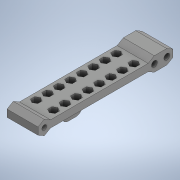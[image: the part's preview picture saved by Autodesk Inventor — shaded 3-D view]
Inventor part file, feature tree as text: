
AUTODESK INVENTOR PART (.ipt)
format: ipt  version: 2020 (Build 240168000, 168)  size: 555,008 bytes
history: native  units: in
note: dims shown in document units (in); Inventor stores cm internally (conversion verified against a paired STEP export)
features: sketch x7, extrude x6, projected_geometry x4, plane x2, mirror x1, fillet x1
ambient origin geometry x8: Origin, YZ Plane, XZ Plane, XY Plane, X Axis, Y Axis, Z Axis, Center Point
bodies: Solid1 (feature_tree)
feature tree (21):
  extrude  "Extrusion1"  Depth=3.4256in
  plane  "Work Plane1"
  extrude  "Extrusion2"  Depth=0.7874in
  sketch  "Sketch4"  dims[d4=0.0in d5=0.0906in]
  extrude  "Extrusion4"  Depth=0.0906in
  plane  "Work Plane2"
  extrude  "Extrusion6"  Depth=3.1106in
  mirror  "Mirror2"
  extrude  "Extrusion7"  Depth=0.315in
  extrude  "Extrusion8"  Depth=0.2362in
  fillet  "Fillet1"  [1 undecoded]
  sketch  "Sketch1"  dims[d0=0.1818in d1=3.4256in]
  sketch  "Sketch2"  dims[d2=0.122in d3=0.7874in]
  sketch  "Sketch5"  dims[d6=0.7874in d7=0.0in d28=3.1106in]
  sketch  "Sketch7"  dims[d29=0.315in d31=0.315in]
  projected_geometry  "Projected Loop7"
  projected_geometry  "Projected Loop8"
  sketch  "Sketch8"  dims[d33=0.1476in d34=0.2362in d35=0.0in]
  projected_geometry  "Projected Loop9"
  sketch  "Sketch10"  dims[d38=0.315in d39=0.2756in d40=-0.3092in d41=0.0787in d42=0.0787in d43=0.0787in d44=3.1496in d46=0.2913in d47=0.3937in d49=0.3937in d51=3.1496in d53=0.2913in d54=0.3937in d56=0.3937in d58=0.0in d59=0.0in d60=1.0994in d61=0.1378in d63=1.1811in d64=0.1575in d65=0.0in d66=0.126in d67=0.1575in]
  projected_geometry  "Projected Loop10"
note: 1 required parameter value undecoded (feature->parameter linkage not recoverable at this tier; creation-order binding heuristic only, values carry confidence <= 0.55)
